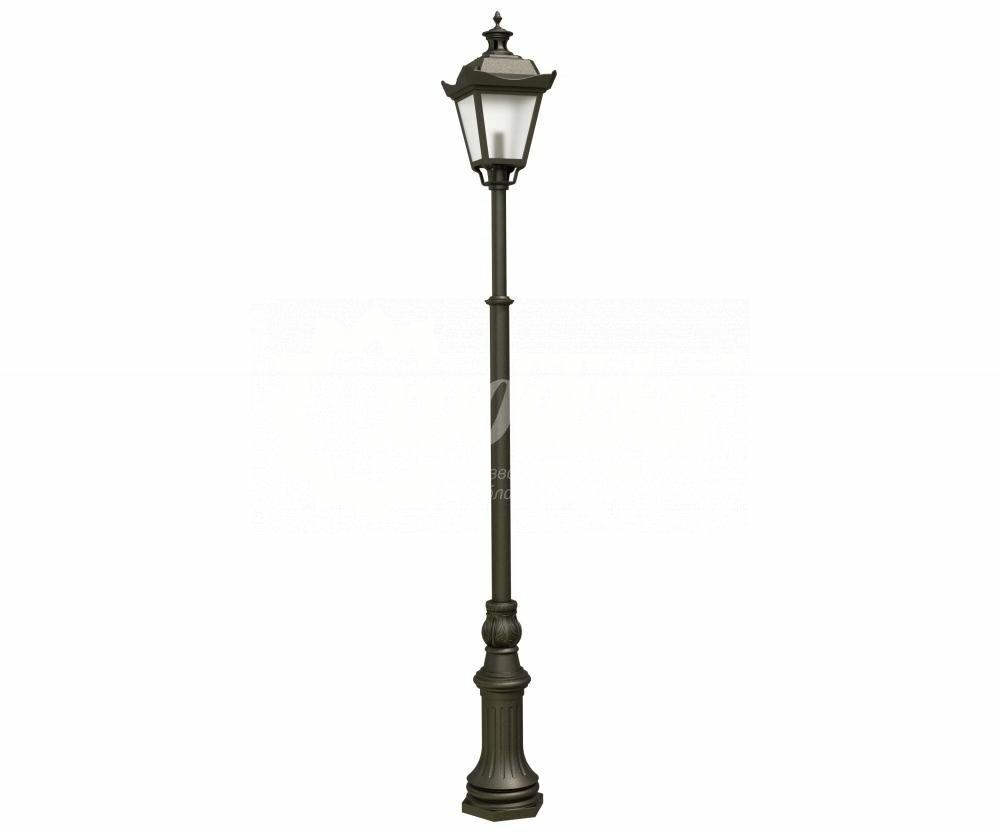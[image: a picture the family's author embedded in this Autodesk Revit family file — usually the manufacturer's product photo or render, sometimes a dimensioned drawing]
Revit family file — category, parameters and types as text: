
# Revit family: Фонарь уличный «Адмирал - 1» со светильником Арт 7467
name_source: partatom
category: Антураж
revit_build: Autodesk Revit 2018 (Build: 20180423_1000(x64)
units: mm (PartAtom-declared; Revit-internal decimal feet)

## family parameters
Всегда вертикально = Да
Источник визуального образа = Геометрия семейства
На основе рабочей плоскости = Нет
Общий = Нет
При загрузке вырезать с полостями = Нет
Точка расчета площади = Нет

## types (6) — shared parameters
URL = https://hobbyka.ru
Артикул товара = Арт. 7467
Группа модели = Светильники с чугунными опорами
Длина = 370 мм
Изготовитель = ООО «Хоббика»
Изображение типоразмера = Фонарь уличный «Адмирал - 1» со светильником Арт 7467.jpg
Материал изделия = Сталь, поликарбонат
Цвет основания = Сталь
Цвет столба = Нержавейка
Ширина = 370 мм

## per-type parameters (varying)
| type | Версия 3,108 м | Версия 3,608 м | Версия 4,108 м | Версия 4,608 м | Версия 5,108 м | Высота | Высота стоба | Описание |
| Версия 3,108 м | Да | Нет | Нет | Нет | Нет | 3108 мм | 1808 мм | Фонарь уличный «Адмирал - 1» со светильником. Версия 3,108 м |
| Версия 3,608 м | Нет | Да | Нет | Нет | Нет | 3608 мм | 2308 мм | Фонарь уличный «Адмирал - 1» со светильником. Версия 3,608 м |
| Версия 4,108 м | Нет | Нет | Да | Нет | Нет | 4108 мм | 2808 мм | Фонарь уличный «Адмирал - 1» со светильником. Версия 4,108 м |
| Версия 4,608 м | Нет | Нет | Нет | Да | Нет | 4608 мм | 3308 мм | Фонарь уличный «Адмирал - 1» со светильником. Версия 4,608 м |
| Версия 5,108 м | Нет | Нет | Нет | Нет | Да | 5108 мм | 3808 мм | Фонарь уличный «Адмирал - 1» со светильником. Версия 5,108 м |
| Версия 5,608 м | Нет | Нет | Нет | Нет | Нет | 5608 мм | 4308 мм | Фонарь уличный «Адмирал - 1» со светильником. Версия 5,608 м |
